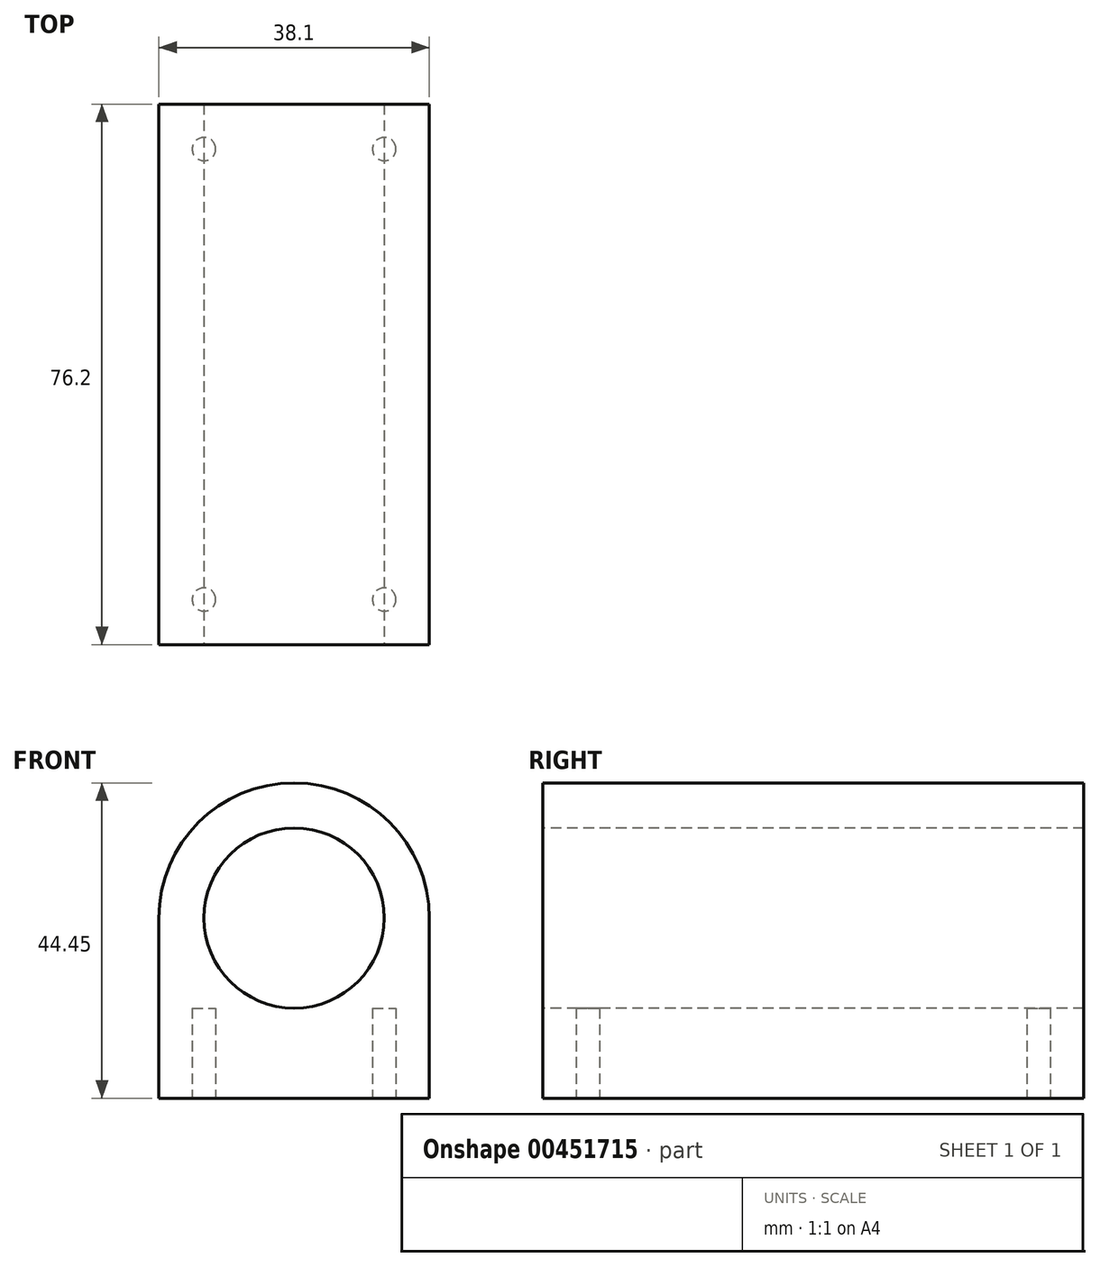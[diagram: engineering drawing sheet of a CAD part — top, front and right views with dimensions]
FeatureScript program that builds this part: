
annotation { "Feature Type Name" : "Feature", "Feature Type Description" : "" }
export const myFeature = defineFeature(function(context is Context, id is Id, definition is map)
    precondition{}
    {
        {
            var Q0;
            Q0=qCreatedBy(makeId("Front.planeOp"),FACE);
            var sketch = newSketch(context, id + "F0", { "sketchPlane" : qUnion([Q0])});
            skLineSegment(sketch, "E0.top", {"start": v(-19.05, 0) * mm, "end": v(19.05, 0) * mm});
            skLineSegment(sketch, "E0.left", {"start": v(-19.05, 25.4) * mm, "end": v(-19.05, 0) * mm});
            skLineSegment(sketch, "E0.right", {"start": v(19.05, 25.4) * mm, "end": v(19.05, 0) * mm});
            skArc(sketch, "E1", {"start": v(19.05, 25.4) * mm, "mid": v(0, 44.45) * mm, "end": v(-19.05, 25.4) * mm});
            skSolve(sketch);
        }
        {
            var Q0;
            Q0 = qSketchRegion(id + "F0", true);
            extrude(context, id + "F1", {"entities" : qUnion([Q0]), "endBound" : BoundingType.SYMMETRIC, "depth" : 76.2 * mm});
        }
        {
            var Q0;
            Q0=makeQuery(id+"F1.opExtrude","CAP_FACE",FACE,{"disambiguationData":[OSD([sQuery(id+"F0.wireOp",EDGE,"E0.top"),sQuery(id+"F0.wireOp",EDGE,"E0.left"),sQuery(id+"F0.wireOp",EDGE,"E0.right"),sQuery(id+"F0.wireOp",EDGE,"E1")])],"isStart":false});
            var sketch = newSketch(context, id + "F2", { "sketchPlane" : qUnion([Q0])});
            skCircle(sketch, "E2", {"center": v(0, 25.4) * mm, "radius": 12.7 * mm});
            skSolve(sketch);
        }
        {
            var Q0;
            Q0 = qSketchRegion(id + "F2", true);
            extrude(context, id + "F3", {"entities" : qUnion([Q0]), "operationType" : NewBodyOperationType.REMOVE, "oppositeDirection" : true, "depth" : 101.35 * mm});
        }
        {
            var Q0;
            Q0=makeQuery(id+"F1.opExtrude","SWEPT_FACE",FACE,{"disambiguationData":[OSD([sQuery(id+"F0.wireOp",EDGE,"E0.top")])]});
            var sketch = newSketch(context, id + "F4", { "sketchPlane" : qUnion([Q0])});
            skLineSegment(sketch, "E3", {"start": v(-19.05, 0) * mm, "end": v(19.05, 0) * mm});
            skLineSegment(sketch, "E4", {"start": v(0, 38.1) * mm, "end": v(0, 0) * mm});
            skCircle(sketch, "E5", {"center": v(12.7, 31.75) * mm, "radius": 1.65 * mm});
            skCircle(sketch, "E6.MirrorC", {"center": v(-12.7, 31.75) * mm, "radius": 1.65 * mm});
            skCircle(sketch, "E7.MirrorC", {"center": v(-12.7, -31.75) * mm, "radius": 1.65 * mm});
            skCircle(sketch, "E8.MirrorC", {"center": v(12.7, -31.75) * mm, "radius": 1.65 * mm});
            skSolve(sketch);
        }
        {
            var Q0;
            Q0 = qSketchRegion(id + "F4", true);
            extrude(context, id + "F5", {"entities" : qUnion([Q0]), "operationType" : NewBodyOperationType.REMOVE, "oppositeDirection" : true, "depth" : 12.7 * mm});
        }
    });
